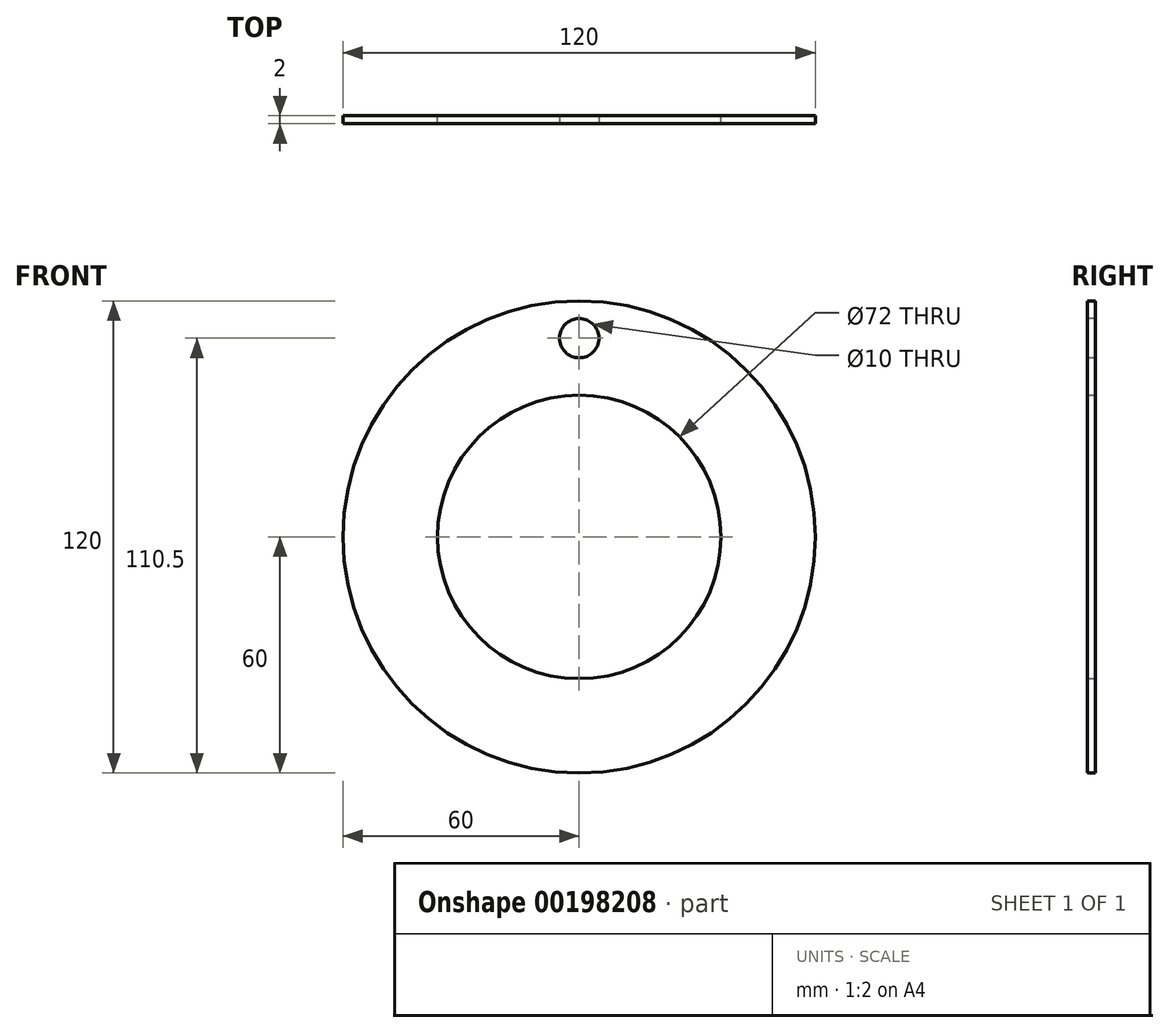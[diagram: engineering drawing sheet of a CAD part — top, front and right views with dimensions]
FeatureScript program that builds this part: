
annotation { "Feature Type Name" : "Feature", "Feature Type Description" : "" }
export const myFeature = defineFeature(function(context is Context, id is Id, definition is map)
    precondition{}
    {
        {
            var Q0;
            Q0=qCreatedBy(makeId("Front.planeOp"),FACE);
            var sketch = newSketch(context, id + "F0", { "sketchPlane" : qUnion([Q0])});
            skCircle(sketch, "E0", {"center": v(0, 0) * mm, "radius": 60 * mm});
            skCircle(sketch, "E1", {"center": v(0, 0) * mm, "radius": 36 * mm});
            skSolve(sketch);
        }
        {
            var Q0;
            Q0=makeQuery(id+"F0.imprint","IMPRINT",FACE,{"disambiguationData":[TD([[makeQuery(id+"F0.imprint","IMPRINT",EDGE,{"derivedFrom":sQuery(id+"F0.wireOp",EDGE,"E0")}),1.0]])]});
            extrude(context, id + "F1", {"entities" : qUnion([Q0]), "depth" : 2 * mm});
        }
        {
            var Q0;
            Q0=makeQuery(id+"F1.opExtrude","CAP_FACE",FACE,{"disambiguationData":[OSD([sQuery(id+"F0.wireOp",EDGE,"E0"),sQuery(id+"F0.wireOp",EDGE,"E1")])],"isStart":false});
            var sketch = newSketch(context, id + "F2", { "sketchPlane" : qUnion([Q0])});
            skCircle(sketch, "E2", {"center": v(0, 0) * mm, "radius": 50.5 * mm, "construction": true});
            skCircle(sketch, "E3", {"center": v(0, 50.5) * mm, "radius": 5 * mm});
            skSolve(sketch);
        }
        {
            var Q0;
            Q0=makeQuery(id+"F2.imprint","IMPRINT",FACE,{"disambiguationData":[TD([[makeQuery(id+"F2.imprint","IMPRINT",EDGE,{"derivedFrom":sQuery(id+"F2.wireOp",EDGE,"E3")}),1.0]])]});
            var Q1;
            Q1=sQuery(id+"F2.wireOp",EDGE,"E3");
            extrude(context, id + "F3", {"entities" : qUnion([Q0]), "operationType" : NewBodyOperationType.REMOVE, "surfaceEntities" : qUnion([Q1]), "endBound" : BoundingType.THROUGH_ALL, "oppositeDirection" : true, "depth" : 25 * mm});
        }
    });
